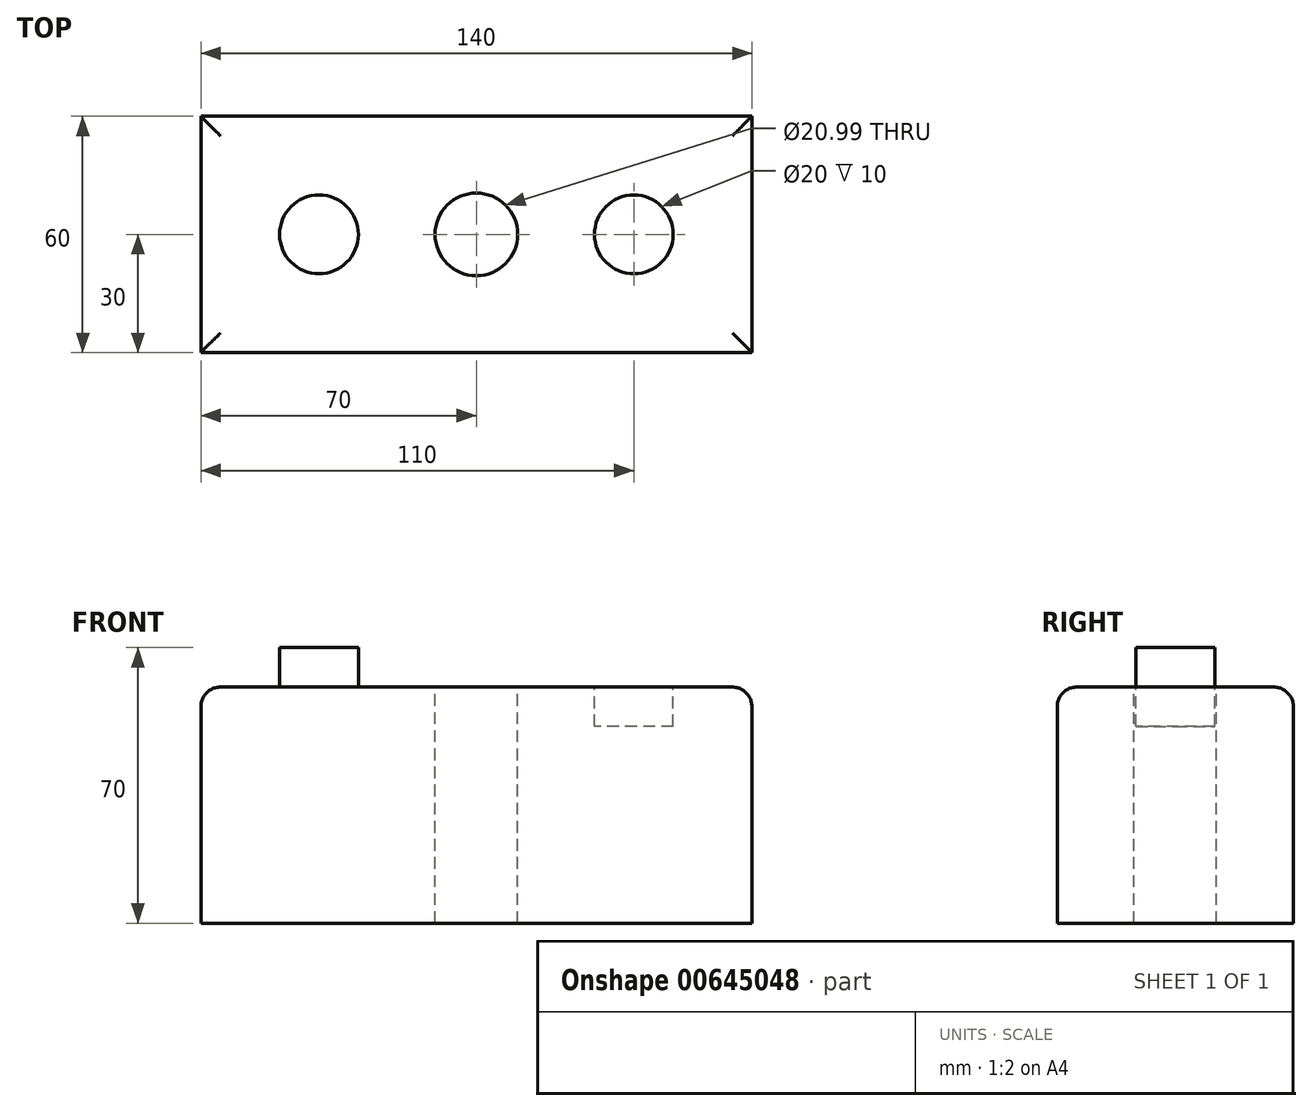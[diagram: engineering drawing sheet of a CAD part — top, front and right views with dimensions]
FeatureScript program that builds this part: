
annotation { "Feature Type Name" : "Feature", "Feature Type Description" : "" }
export const myFeature = defineFeature(function(context is Context, id is Id, definition is map)
    precondition{}
    {
        {
            var Q0;
            Q0=qCreatedBy(makeId("Top.planeOp"),FACE);
            var sketch = newSketch(context, id + "F0", { "sketchPlane" : qUnion([Q0])});
            skLineSegment(sketch, "E0.bottom", {"start": v(70, -30) * mm, "end": v(-70, -30) * mm});
            skLineSegment(sketch, "E0.top", {"start": v(70, 30) * mm, "end": v(-70, 30) * mm});
            skLineSegment(sketch, "E0.left", {"start": v(70, -30) * mm, "end": v(70, 30) * mm});
            skLineSegment(sketch, "E0.right", {"start": v(-70, -30) * mm, "end": v(-70, 30) * mm});
            skPoint(sketch, "E0.middle", {"position": v(0, 0) * mm});
            skSolve(sketch);
        }
        {
            var Q0;
            Q0 = qSketchRegion(id + "F0", true);
            extrude(context, id + "F1", {"entities" : qUnion([Q0]), "depth" : 60 * mm, "offsetDistance" : 25 * mm});
        }
        {
            var Q0;
            Q0=makeQuery(id+"F1.opExtrude","CAP_FACE",FACE,{"disambiguationData":[OSD([sQuery(id+"F0.wireOp",EDGE,"E0.bottom"),sQuery(id+"F0.wireOp",EDGE,"E0.top"),sQuery(id+"F0.wireOp",EDGE,"E0.left"),sQuery(id+"F0.wireOp",EDGE,"E0.right")])],"isStart":false});
            var sketch = newSketch(context, id + "F2", { "sketchPlane" : qUnion([Q0])});
            skCircle(sketch, "E1", {"center": v(-40, 0) * mm, "radius": 10 * mm});
            skSolve(sketch);
        }
        {
            var Q0;
            Q0=makeQuery(id+"F2.imprint","IMPRINT",FACE,{"disambiguationData":[TD([[makeQuery(id+"F2.imprint","IMPRINT",EDGE,{"derivedFrom":sQuery(id+"F2.wireOp",EDGE,"E1")}),-1.0]])]});
            var sketch = newSketch(context, id + "F3", { "sketchPlane" : qUnion([Q0])});
            skCircle(sketch, "E2", {"center": v(40, 0) * mm, "radius": 10 * mm});
            skSolve(sketch);
        }
        {
            var Q0;
            Q0=makeQuery(id+"F2.imprint","IMPRINT",FACE,{"disambiguationData":[TD([[makeQuery(id+"F2.imprint","IMPRINT",EDGE,{"derivedFrom":sQuery(id+"F2.wireOp",EDGE,"E1")}),-1.0]])]});
            var sketch = newSketch(context, id + "F4", { "sketchPlane" : qUnion([Q0])});
            skCircle(sketch, "E3", {"center": v(0, 0) * mm, "radius": 10.5 * mm});
            skSolve(sketch);
        }
        {
            var Q0;
            Q0 = qSketchRegion(id + "F2", true);
            extrude(context, id + "F5", {"entities" : qUnion([Q0]), "operationType" : NewBodyOperationType.ADD, "depth" : 10 * mm, "offsetDistance" : 25 * mm});
        }
        {
            var Q0;
            Q0 = qSketchRegion(id + "F4", true);
            extrude(context, id + "F6", {"entities" : qUnion([Q0]), "operationType" : NewBodyOperationType.REMOVE, "oppositeDirection" : true, "depth" : 69.2 * mm, "offsetDistance" : 25 * mm});
        }
        {
            var Q0;
            Q0 = qSketchRegion(id + "F3", true);
            extrude(context, id + "F7", {"entities" : qUnion([Q0]), "operationType" : NewBodyOperationType.REMOVE, "oppositeDirection" : true, "depth" : 10 * mm, "offsetDistance" : 25 * mm});
        }
        {
            var Q0;
            Q0=makeQuery(id+"F1.opExtrude","CAP_EDGE",EDGE,{"disambiguationData":[OSD([sQuery(id+"F0.wireOp",EDGE,"E0.right")])],"isStart":false});
            var Q1;
            Q1=makeQuery(id+"F1.opExtrude","CAP_EDGE",EDGE,{"disambiguationData":[OSD([sQuery(id+"F0.wireOp",EDGE,"E0.bottom")])],"isStart":false});
            var Q2;
            Q2=makeQuery(id+"F1.opExtrude","CAP_EDGE",EDGE,{"disambiguationData":[OSD([sQuery(id+"F0.wireOp",EDGE,"E0.left")])],"isStart":false});
            var Q3;
            Q3=makeQuery(id+"F1.opExtrude","CAP_EDGE",EDGE,{"disambiguationData":[OSD([sQuery(id+"F0.wireOp",EDGE,"E0.top")])],"isStart":false});
            fillet(context, id + "F8", {"entities" : qUnion([Q0, Q1, Q2, Q3]), "radius" : 5 * mm, "tangentPropagation" : true, "allowEdgeOverflow" : false});
        }
    });
